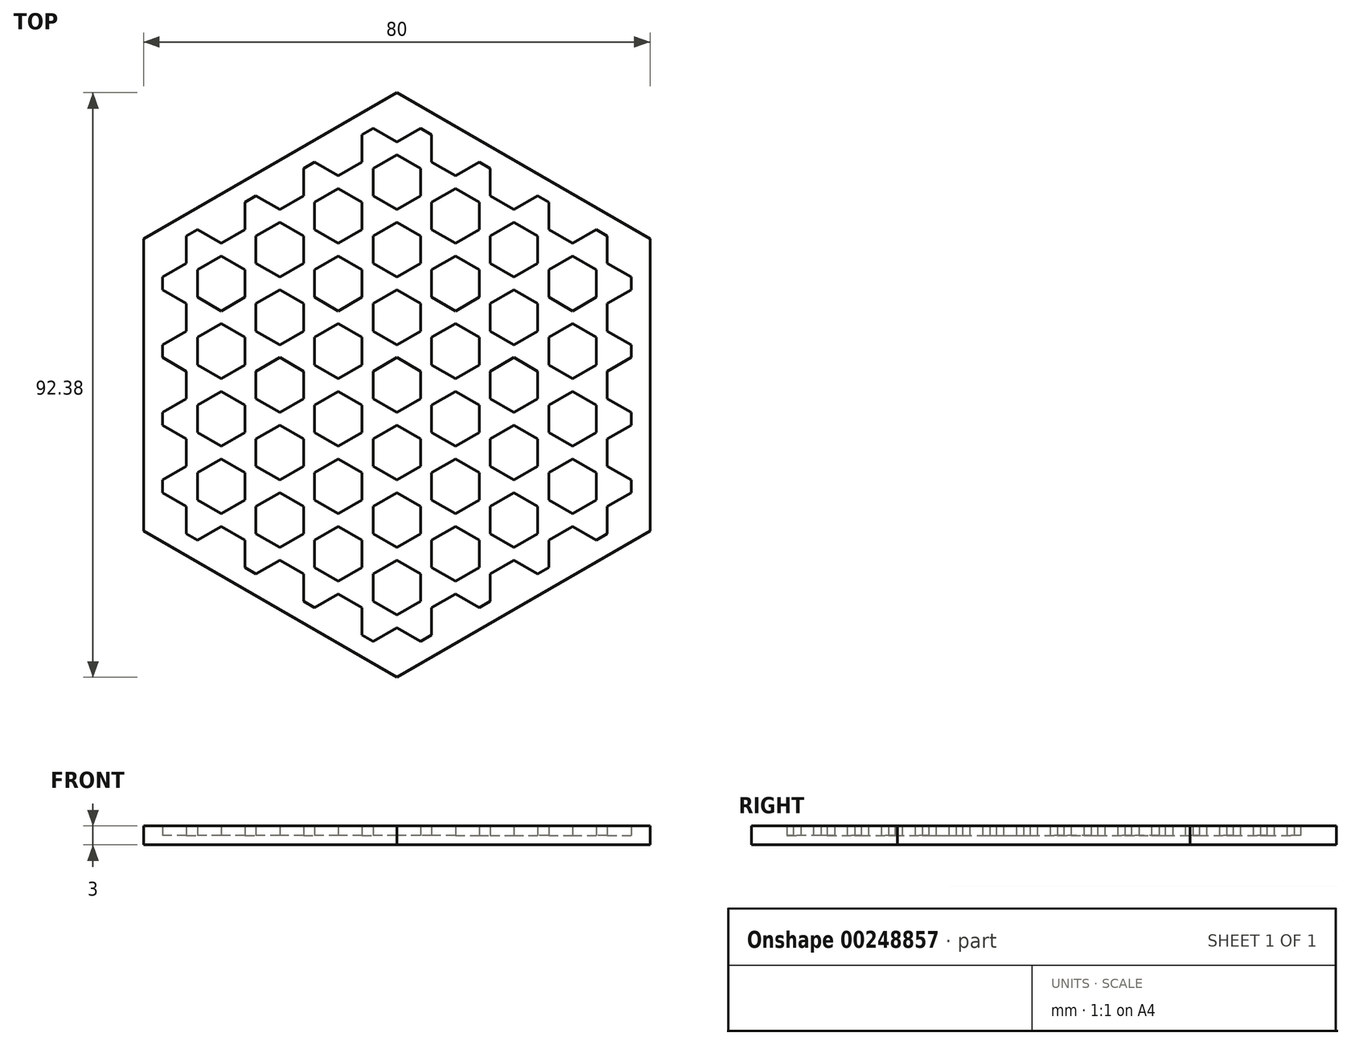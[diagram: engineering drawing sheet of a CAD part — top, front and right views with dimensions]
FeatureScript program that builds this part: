
annotation { "Feature Type Name" : "Feature", "Feature Type Description" : "" }
export const myFeature = defineFeature(function(context is Context, id is Id, definition is map)
    precondition{}
    {
        {
            var Q0;
            Q0=qCreatedBy(makeId("Top.planeOp"),FACE);
            var sketch = newSketch(context, id + "F0", { "sketchPlane" : qUnion([Q0])});
            skCircle(sketch, "E0.cCircle", {"center": v(0, 0) * mm, "radius": 40 * mm, "construction": true});
            skLineSegment(sketch, "E0.0", {"start": v(40, 23.1) * mm, "end": v(40, -23.1) * mm});
            skLineSegment(sketch, "E0.1", {"start": v(40, -23.1) * mm, "end": v(0, -46.19) * mm});
            skLineSegment(sketch, "E0.2", {"start": v(0, -46.19) * mm, "end": v(-40, -23.1) * mm});
            skLineSegment(sketch, "E0.3", {"start": v(-40, -23.1) * mm, "end": v(-40, 23.1) * mm});
            skLineSegment(sketch, "E0.4", {"start": v(-40, 23.1) * mm, "end": v(0, 46.19) * mm});
            skLineSegment(sketch, "E0.5", {"start": v(0, 46.19) * mm, "end": v(40, 23.1) * mm});
            skPoint(sketch, "E0.0.midPoint", {"position": v(40, 0) * mm});
            skSolve(sketch);
        }
        {
            var Q0;
            Q0=makeQuery(id+"F0.imprint","IMPRINT",FACE,{"disambiguationData":[TD([[makeQuery(id+"F0.imprint","IMPRINT",EDGE,{"derivedFrom":sQuery(id+"F0.wireOp",EDGE,"E0.0")}),-1.0]])]});
            extrude(context, id + "F3", {"entities" : qUnion([Q0]), "depth" : 3 * mm});
        }
        {
            var Q0;
            Q0=makeQuery(id+"F3.opExtrude","CAP_FACE",FACE,{"disambiguationData":[OSD([sQuery(id+"F0.wireOp",EDGE,"E0.0"),sQuery(id+"F0.wireOp",EDGE,"E0.1"),sQuery(id+"F0.wireOp",EDGE,"E0.2"),sQuery(id+"F0.wireOp",EDGE,"E0.3"),sQuery(id+"F0.wireOp",EDGE,"E0.4"),sQuery(id+"F0.wireOp",EDGE,"E0.5")])],"isStart":false});
            var sketch = newSketch(context, id + "F1", { "sketchPlane" : qUnion([Q0])});
            skCircle(sketch, "E1.cCircle", {"center": v(0, 0) * mm, "radius": 37 * mm, "construction": true});
            skPoint(sketch, "E1.cCircle.perimeterSnap0", {"position": v(40, 0) * mm});
            skLineSegment(sketch, "E1.0", {"start": v(37, 21.36) * mm, "end": v(37, -21.36) * mm});
            skLineSegment(sketch, "E1.1", {"start": v(37, -21.36) * mm, "end": v(0, -42.72) * mm});
            skLineSegment(sketch, "E1.2", {"start": v(0, -42.72) * mm, "end": v(-37, -21.36) * mm});
            skLineSegment(sketch, "E1.3", {"start": v(-37, -21.36) * mm, "end": v(-37, 21.36) * mm});
            skLineSegment(sketch, "E1.4", {"start": v(-37, 21.36) * mm, "end": v(0, 42.72) * mm});
            skLineSegment(sketch, "E1.5", {"start": v(0, 42.72) * mm, "end": v(37, 21.36) * mm});
            skPoint(sketch, "E1.0.midPoint", {"position": v(37, 0) * mm});
            skPoint(sketch, "E1.0.midPoint.positionSnap0", {"position": v(40, 0) * mm});
            skSolve(sketch);
        }
        {
            var Q0;
            Q0=makeQuery(id+"F1.imprint","IMPRINT",FACE,{"disambiguationData":[TD([[makeQuery(id+"F1.imprint","IMPRINT",EDGE,{"derivedFrom":sQuery(id+"F1.wireOp",EDGE,"E1.0")}),-1.0]])]});
            extrude(context, id + "F4", {"entities" : qUnion([Q0]), "operationType" : NewBodyOperationType.REMOVE, "oppositeDirection" : true, "depth" : 1.5 * mm});
        }
        {
            var Q0;
            Q0=makeQuery(id+"F4.boolean.opBoolean","COPY",FACE,{"derivedFrom":makeQuery(id+"F4.opExtrude","CAP_FACE",FACE,{"disambiguationData":[OSD([sQuery(id+"F1.wireOp",EDGE,"E1.0"),sQuery(id+"F1.wireOp",EDGE,"E1.1"),sQuery(id+"F1.wireOp",EDGE,"E1.2"),sQuery(id+"F1.wireOp",EDGE,"E1.3"),sQuery(id+"F1.wireOp",EDGE,"E1.4"),sQuery(id+"F1.wireOp",EDGE,"E1.5")])],"isStart":false})});
            var sketch = newSketch(context, id + "F2", { "sketchPlane" : qUnion([Q0])});
            skLineSegment(sketch, "E2", {"start": v(-32.37, 24.03) * mm, "end": v(-32.37, -24.03) * mm, "construction": true});
            skLineSegment(sketch, "E3", {"start": v(-23.12, 29.37) * mm, "end": v(-23.12, -29.37) * mm, "construction": true});
            skLineSegment(sketch, "E4", {"start": v(-13.88, 34.71) * mm, "end": v(-13.88, -34.71) * mm, "construction": true});
            skLineSegment(sketch, "E5", {"start": v(-4.62, 40.05) * mm, "end": v(-4.62, -40.05) * mm, "construction": true});
            skLineSegment(sketch, "E6", {"start": v(-37, -16.02) * mm, "end": v(4.63, -40.05) * mm, "construction": true});
            skLineSegment(sketch, "E7", {"start": v(13.88, -34.71) * mm, "end": v(-37, -5.34) * mm, "construction": true});
            skLineSegment(sketch, "E8", {"start": v(-37, 5.34) * mm, "end": v(23.12, -29.37) * mm, "construction": true});
            skLineSegment(sketch, "E9", {"start": v(32.37, -24.03) * mm, "end": v(-37, 16.02) * mm, "construction": true});
            skLineSegment(sketch, "E10", {"start": v(-32.37, 24.03) * mm, "end": v(37, -16.02) * mm, "construction": true});
            skLineSegment(sketch, "E11", {"start": v(-23.12, 29.37) * mm, "end": v(37, -5.34) * mm, "construction": true});
            skPoint(sketch, "E11.endSnap0", {"position": v(58.53, 6.8) * mm});
            skLineSegment(sketch, "E12", {"start": v(-13.88, 34.71) * mm, "end": v(37, 5.34) * mm, "construction": true});
            skLineSegment(sketch, "E13", {"start": v(-4.63, 40.05) * mm, "end": v(37, 16.02) * mm, "construction": true});
            skLineSegment(sketch, "E14", {"start": v(4.63, -40.05) * mm, "end": v(4.62, 40.05) * mm, "construction": true});
            skLineSegment(sketch, "E15", {"start": v(13.88, -34.71) * mm, "end": v(13.87, 34.71) * mm, "construction": true});
            skLineSegment(sketch, "E16", {"start": v(23.12, -29.37) * mm, "end": v(23.12, 29.37) * mm, "construction": true});
            skLineSegment(sketch, "E17", {"start": v(32.37, -24.03) * mm, "end": v(32.37, 24.03) * mm, "construction": true});
            skLineSegment(sketch, "E18", {"start": v(-37, 16.02) * mm, "end": v(4.63, 40.05) * mm, "construction": true});
            skLineSegment(sketch, "E19", {"start": v(-37, 5.34) * mm, "end": v(13.88, 34.71) * mm, "construction": true});
            skLineSegment(sketch, "E20", {"start": v(-37, -5.34) * mm, "end": v(23.12, 29.37) * mm, "construction": true});
            skLineSegment(sketch, "E21", {"start": v(-37, -16.02) * mm, "end": v(32.37, 24.03) * mm, "construction": true});
            skLineSegment(sketch, "E22", {"start": v(-32.37, -24.03) * mm, "end": v(37, 16.02) * mm, "construction": true});
            skLineSegment(sketch, "E23", {"start": v(37, 5.34) * mm, "end": v(-23.12, -29.37) * mm, "construction": true});
            skLineSegment(sketch, "E24", {"start": v(-13.88, -34.71) * mm, "end": v(37, -5.34) * mm, "construction": true});
            skLineSegment(sketch, "E25", {"start": v(-4.62, -40.05) * mm, "end": v(37, -16.02) * mm, "construction": true});
            skSolve(sketch);
        }
        {
            var Q0;
            Q0=makeQuery(id+"F4.boolean.opBoolean","COPY",FACE,{"derivedFrom":makeQuery(id+"F4.opExtrude","CAP_FACE",FACE,{"disambiguationData":[OSD([sQuery(id+"F1.wireOp",EDGE,"E1.0"),sQuery(id+"F1.wireOp",EDGE,"E1.1"),sQuery(id+"F1.wireOp",EDGE,"E1.2"),sQuery(id+"F1.wireOp",EDGE,"E1.3"),sQuery(id+"F1.wireOp",EDGE,"E1.4"),sQuery(id+"F1.wireOp",EDGE,"E1.5")])],"isStart":false})});
            var sketch = newSketch(context, id + "F5", { "sketchPlane" : qUnion([Q0])});
            skCircle(sketch, "E26.cCircle", {"center": v(0, 0) * mm, "radius": 3.75 * mm, "construction": true});
            skLineSegment(sketch, "E26.0", {"start": v(3.75, 2.17) * mm, "end": v(3.75, -2.17) * mm});
            skLineSegment(sketch, "E26.1", {"start": v(3.75, -2.17) * mm, "end": v(0, -4.33) * mm});
            skLineSegment(sketch, "E26.2", {"start": v(0, -4.33) * mm, "end": v(-3.75, -2.17) * mm});
            skLineSegment(sketch, "E26.3", {"start": v(-3.75, -2.17) * mm, "end": v(-3.75, 2.17) * mm});
            skLineSegment(sketch, "E26.4", {"start": v(-3.75, 2.17) * mm, "end": v(0, 4.33) * mm});
            skLineSegment(sketch, "E26.5", {"start": v(0, 4.33) * mm, "end": v(3.75, 2.17) * mm});
            skPoint(sketch, "E26.0.midPoint", {"position": v(3.75, 0) * mm});
            skCircle(sketch, "E27.cCircle", {"center": v(0, -10.68) * mm, "radius": 3.75 * mm, "construction": true});
            skLineSegment(sketch, "E27.0", {"start": v(3.75, -8.52) * mm, "end": v(3.75, -12.85) * mm});
            skLineSegment(sketch, "E27.1", {"start": v(3.75, -12.85) * mm, "end": v(0, -15.01) * mm});
            skLineSegment(sketch, "E27.2", {"start": v(0, -15.01) * mm, "end": v(-3.75, -12.85) * mm});
            skLineSegment(sketch, "E27.3", {"start": v(-3.75, -12.85) * mm, "end": v(-3.75, -8.52) * mm});
            skLineSegment(sketch, "E27.4", {"start": v(-3.75, -8.52) * mm, "end": v(0, -6.35) * mm});
            skLineSegment(sketch, "E27.5", {"start": v(0, -6.35) * mm, "end": v(3.75, -8.52) * mm});
            skPoint(sketch, "E27.0.midPoint", {"position": v(3.75, -10.68) * mm});
            skCircle(sketch, "E28.cCircle", {"center": v(0, -21.36) * mm, "radius": 3.75 * mm, "construction": true});
            skLineSegment(sketch, "E28.0", {"start": v(3.75, -19.2) * mm, "end": v(3.75, -23.53) * mm});
            skLineSegment(sketch, "E28.1", {"start": v(3.75, -23.53) * mm, "end": v(0, -25.7) * mm});
            skLineSegment(sketch, "E28.2", {"start": v(0, -25.7) * mm, "end": v(-3.75, -23.53) * mm});
            skLineSegment(sketch, "E28.3", {"start": v(-3.75, -23.53) * mm, "end": v(-3.75, -19.2) * mm});
            skLineSegment(sketch, "E28.4", {"start": v(-3.75, -19.2) * mm, "end": v(0, -17.03) * mm});
            skLineSegment(sketch, "E28.5", {"start": v(0, -17.03) * mm, "end": v(3.75, -19.2) * mm});
            skPoint(sketch, "E28.0.midPoint", {"position": v(3.75, -21.36) * mm});
            skCircle(sketch, "E29.cCircle", {"center": v(0, -32.04) * mm, "radius": 3.75 * mm, "construction": true});
            skLineSegment(sketch, "E29.0", {"start": v(3.75, -29.88) * mm, "end": v(3.75, -34.2) * mm});
            skLineSegment(sketch, "E29.1", {"start": v(3.75, -34.2) * mm, "end": v(0, -36.37) * mm});
            skLineSegment(sketch, "E29.2", {"start": v(0, -36.37) * mm, "end": v(-3.75, -34.2) * mm});
            skLineSegment(sketch, "E29.3", {"start": v(-3.75, -34.2) * mm, "end": v(-3.75, -29.88) * mm});
            skLineSegment(sketch, "E29.4", {"start": v(-3.75, -29.88) * mm, "end": v(0, -27.71) * mm});
            skLineSegment(sketch, "E29.5", {"start": v(0, -27.71) * mm, "end": v(3.75, -29.88) * mm});
            skPoint(sketch, "E29.0.midPoint", {"position": v(3.75, -32.04) * mm});
            skCircle(sketch, "E30.cCircle", {"center": v(0, -42.72) * mm, "radius": 3.75 * mm, "construction": true});
            skLineSegment(sketch, "E30.0", {"start": v(3.75, -40.56) * mm, "end": v(3.75, -44.89) * mm});
            skLineSegment(sketch, "E30.1", {"start": v(3.75, -44.89) * mm, "end": v(0, -47.05) * mm});
            skLineSegment(sketch, "E30.2", {"start": v(0, -47.05) * mm, "end": v(-3.75, -44.89) * mm});
            skLineSegment(sketch, "E30.3", {"start": v(-3.75, -44.89) * mm, "end": v(-3.75, -40.56) * mm});
            skLineSegment(sketch, "E30.4", {"start": v(-3.75, -40.56) * mm, "end": v(0, -38.4) * mm});
            skLineSegment(sketch, "E30.5", {"start": v(0, -38.4) * mm, "end": v(3.75, -40.56) * mm});
            skPoint(sketch, "E30.0.midPoint", {"position": v(3.75, -42.72) * mm});
            skLineSegment(sketch, "E31", {"start": v(-37, -5.34) * mm, "end": v(-37, -16.02) * mm, "construction": true});
            skLineSegment(sketch, "E32", {"start": v(-37, -10.68) * mm, "end": v(37, -10.68) * mm, "construction": true});
            skLineSegment(sketch, "E33", {"start": v(0, 0) * mm, "end": v(0, -10.68) * mm, "construction": true});
            skLineSegment(sketch, "E34", {"start": v(0, -10.68) * mm, "end": v(0, -21.36) * mm, "construction": true});
            skLineSegment(sketch, "E35", {"start": v(0, -21.36) * mm, "end": v(0, -32.04) * mm, "construction": true});
            skLineSegment(sketch, "E36", {"start": v(0, -32.04) * mm, "end": v(0, -42.72) * mm, "construction": true});
            skCircle(sketch, "E37.cCircle", {"center": v(0, 10.68) * mm, "radius": 3.75 * mm, "construction": true});
            skLineSegment(sketch, "E37.0", {"start": v(3.75, 12.85) * mm, "end": v(3.75, 8.52) * mm});
            skLineSegment(sketch, "E37.1", {"start": v(3.75, 8.52) * mm, "end": v(0, 6.35) * mm});
            skLineSegment(sketch, "E37.2", {"start": v(0, 6.35) * mm, "end": v(-3.75, 8.52) * mm});
            skLineSegment(sketch, "E37.3", {"start": v(-3.75, 8.52) * mm, "end": v(-3.75, 12.85) * mm});
            skLineSegment(sketch, "E37.4", {"start": v(-3.75, 12.85) * mm, "end": v(0, 15.01) * mm});
            skLineSegment(sketch, "E37.5", {"start": v(0, 15.01) * mm, "end": v(3.75, 12.85) * mm});
            skPoint(sketch, "E37.0.midPoint", {"position": v(3.75, 10.68) * mm});
            skCircle(sketch, "E38.cCircle", {"center": v(0, 21.36) * mm, "radius": 3.75 * mm, "construction": true});
            skLineSegment(sketch, "E38.0", {"start": v(3.75, 23.53) * mm, "end": v(3.75, 19.2) * mm});
            skLineSegment(sketch, "E38.1", {"start": v(3.75, 19.2) * mm, "end": v(0, 17.03) * mm});
            skLineSegment(sketch, "E38.2", {"start": v(0, 17.03) * mm, "end": v(-3.75, 19.2) * mm});
            skLineSegment(sketch, "E38.3", {"start": v(-3.75, 19.2) * mm, "end": v(-3.75, 23.53) * mm});
            skLineSegment(sketch, "E38.4", {"start": v(-3.75, 23.53) * mm, "end": v(0, 25.7) * mm});
            skLineSegment(sketch, "E38.5", {"start": v(0, 25.7) * mm, "end": v(3.75, 23.53) * mm});
            skPoint(sketch, "E38.0.midPoint", {"position": v(3.75, 21.36) * mm});
            skCircle(sketch, "E39.cCircle", {"center": v(0, 32.04) * mm, "radius": 3.75 * mm, "construction": true});
            skLineSegment(sketch, "E39.0", {"start": v(3.75, 34.2) * mm, "end": v(3.75, 29.88) * mm});
            skLineSegment(sketch, "E39.1", {"start": v(3.75, 29.88) * mm, "end": v(0, 27.71) * mm});
            skLineSegment(sketch, "E39.2", {"start": v(0, 27.71) * mm, "end": v(-3.75, 29.88) * mm});
            skLineSegment(sketch, "E39.3", {"start": v(-3.75, 29.88) * mm, "end": v(-3.75, 34.2) * mm});
            skLineSegment(sketch, "E39.4", {"start": v(-3.75, 34.2) * mm, "end": v(0, 36.37) * mm});
            skLineSegment(sketch, "E39.5", {"start": v(0, 36.37) * mm, "end": v(3.75, 34.2) * mm});
            skPoint(sketch, "E39.0.midPoint", {"position": v(3.75, 32.04) * mm});
            skCircle(sketch, "E40.cCircle", {"center": v(0, 42.72) * mm, "radius": 3.75 * mm, "construction": true});
            skLineSegment(sketch, "E40.0", {"start": v(3.75, 44.89) * mm, "end": v(3.75, 40.56) * mm});
            skLineSegment(sketch, "E40.1", {"start": v(3.75, 40.56) * mm, "end": v(0, 38.4) * mm});
            skLineSegment(sketch, "E40.2", {"start": v(0, 38.4) * mm, "end": v(-3.75, 40.56) * mm});
            skLineSegment(sketch, "E40.3", {"start": v(-3.75, 40.56) * mm, "end": v(-3.75, 44.89) * mm});
            skLineSegment(sketch, "E40.4", {"start": v(-3.75, 44.89) * mm, "end": v(0, 47.05) * mm});
            skLineSegment(sketch, "E40.5", {"start": v(0, 47.05) * mm, "end": v(3.75, 44.89) * mm});
            skPoint(sketch, "E40.0.midPoint", {"position": v(3.75, 42.72) * mm});
            skLineSegment(sketch, "E41", {"start": v(0, 42.72) * mm, "end": v(0, 32.04) * mm, "construction": true});
            skLineSegment(sketch, "E42", {"start": v(0, 21.36) * mm, "end": v(0, 32.04) * mm, "construction": true});
            skLineSegment(sketch, "E43", {"start": v(0, 21.36) * mm, "end": v(0, 10.68) * mm, "construction": true});
            skLineSegment(sketch, "E44", {"start": v(0, 10.68) * mm, "end": v(0, 0) * mm, "construction": true});
            skLineSegment(sketch, "E45", {"start": v(-37, -5.34) * mm, "end": v(37, -5.34) * mm, "construction": true});
            skCircle(sketch, "E46.cCircle", {"center": v(-9.25, -5.34) * mm, "radius": 3.75 * mm, "construction": true});
            skLineSegment(sketch, "E46.0", {"start": v(-5.5, -3.18) * mm, "end": v(-5.5, -7.5) * mm});
            skLineSegment(sketch, "E46.1", {"start": v(-5.5, -7.5) * mm, "end": v(-9.25, -9.67) * mm});
            skLineSegment(sketch, "E46.2", {"start": v(-9.25, -9.67) * mm, "end": v(-13, -7.5) * mm});
            skLineSegment(sketch, "E46.3", {"start": v(-13, -7.5) * mm, "end": v(-13, -3.18) * mm});
            skLineSegment(sketch, "E46.4", {"start": v(-13, -3.18) * mm, "end": v(-9.25, -1.01) * mm});
            skLineSegment(sketch, "E46.5", {"start": v(-9.25, -1.01) * mm, "end": v(-5.5, -3.18) * mm});
            skPoint(sketch, "E46.0.midPoint", {"position": v(-5.5, -5.34) * mm});
            skCircle(sketch, "E47.cCircle", {"center": v(-9.25, -16.02) * mm, "radius": 3.75 * mm, "construction": true});
            skLineSegment(sketch, "E47.0", {"start": v(-13, -18.19) * mm, "end": v(-13, -13.86) * mm});
            skLineSegment(sketch, "E47.1", {"start": v(-13, -13.86) * mm, "end": v(-9.25, -11.7) * mm});
            skLineSegment(sketch, "E47.2", {"start": v(-9.25, -11.7) * mm, "end": v(-5.5, -13.86) * mm});
            skLineSegment(sketch, "E47.3", {"start": v(-5.5, -13.86) * mm, "end": v(-5.5, -18.19) * mm});
            skLineSegment(sketch, "E47.4", {"start": v(-5.5, -18.19) * mm, "end": v(-9.25, -20.35) * mm});
            skLineSegment(sketch, "E47.5", {"start": v(-9.25, -20.35) * mm, "end": v(-13, -18.19) * mm});
            skPoint(sketch, "E47.0.midPoint", {"position": v(-13, -16.02) * mm});
            skCircle(sketch, "E48.cCircle", {"center": v(-9.25, -26.7) * mm, "radius": 3.75 * mm, "construction": true});
            skLineSegment(sketch, "E48.0", {"start": v(-13, -28.87) * mm, "end": v(-13, -24.54) * mm});
            skLineSegment(sketch, "E48.1", {"start": v(-13, -24.54) * mm, "end": v(-9.25, -22.37) * mm});
            skLineSegment(sketch, "E48.2", {"start": v(-9.25, -22.37) * mm, "end": v(-5.5, -24.54) * mm});
            skLineSegment(sketch, "E48.3", {"start": v(-5.5, -24.54) * mm, "end": v(-5.5, -28.87) * mm});
            skLineSegment(sketch, "E48.4", {"start": v(-5.5, -28.87) * mm, "end": v(-9.25, -31.03) * mm});
            skLineSegment(sketch, "E48.5", {"start": v(-9.25, -31.03) * mm, "end": v(-13, -28.87) * mm});
            skPoint(sketch, "E48.0.midPoint", {"position": v(-13, -26.7) * mm});
            skCircle(sketch, "E49.cCircle", {"center": v(-9.25, -37.38) * mm, "radius": 3.75 * mm, "construction": true});
            skLineSegment(sketch, "E49.0", {"start": v(-13, -39.55) * mm, "end": v(-13, -35.22) * mm});
            skLineSegment(sketch, "E49.1", {"start": v(-13, -35.22) * mm, "end": v(-9.25, -33.05) * mm});
            skLineSegment(sketch, "E49.2", {"start": v(-9.25, -33.05) * mm, "end": v(-5.5, -35.22) * mm});
            skLineSegment(sketch, "E49.3", {"start": v(-5.5, -35.22) * mm, "end": v(-5.5, -39.55) * mm});
            skLineSegment(sketch, "E49.4", {"start": v(-5.5, -39.55) * mm, "end": v(-9.25, -41.71) * mm});
            skLineSegment(sketch, "E49.5", {"start": v(-9.25, -41.71) * mm, "end": v(-13, -39.55) * mm});
            skPoint(sketch, "E49.0.midPoint", {"position": v(-13, -37.38) * mm});
            skCircle(sketch, "E50.cCircle", {"center": v(-9.25, 5.34) * mm, "radius": 3.75 * mm, "construction": true});
            skLineSegment(sketch, "E50.0", {"start": v(-13, 3.18) * mm, "end": v(-13, 7.5) * mm});
            skLineSegment(sketch, "E50.1", {"start": v(-13, 7.5) * mm, "end": v(-9.25, 9.67) * mm});
            skLineSegment(sketch, "E50.2", {"start": v(-9.25, 9.67) * mm, "end": v(-5.5, 7.5) * mm});
            skLineSegment(sketch, "E50.3", {"start": v(-5.5, 7.5) * mm, "end": v(-5.5, 3.18) * mm});
            skLineSegment(sketch, "E50.4", {"start": v(-5.5, 3.18) * mm, "end": v(-9.25, 1.01) * mm});
            skLineSegment(sketch, "E50.5", {"start": v(-9.25, 1.01) * mm, "end": v(-13, 3.18) * mm});
            skPoint(sketch, "E50.0.midPoint", {"position": v(-13, 5.34) * mm});
            skCircle(sketch, "E51.cCircle", {"center": v(-9.25, 16.02) * mm, "radius": 3.75 * mm, "construction": true});
            skLineSegment(sketch, "E51.0", {"start": v(-13, 13.86) * mm, "end": v(-13, 18.19) * mm});
            skLineSegment(sketch, "E51.1", {"start": v(-13, 18.19) * mm, "end": v(-9.25, 20.35) * mm});
            skLineSegment(sketch, "E51.2", {"start": v(-9.25, 20.35) * mm, "end": v(-5.5, 18.19) * mm});
            skLineSegment(sketch, "E51.3", {"start": v(-5.5, 18.19) * mm, "end": v(-5.5, 13.86) * mm});
            skLineSegment(sketch, "E51.4", {"start": v(-5.5, 13.86) * mm, "end": v(-9.25, 11.7) * mm});
            skLineSegment(sketch, "E51.5", {"start": v(-9.25, 11.7) * mm, "end": v(-13, 13.86) * mm});
            skPoint(sketch, "E51.0.midPoint", {"position": v(-13, 16.02) * mm});
            skCircle(sketch, "E52.cCircle", {"center": v(-9.25, 26.7) * mm, "radius": 3.75 * mm, "construction": true});
            skLineSegment(sketch, "E52.0", {"start": v(-13, 24.54) * mm, "end": v(-13, 28.87) * mm});
            skLineSegment(sketch, "E52.1", {"start": v(-13, 28.87) * mm, "end": v(-9.25, 31.03) * mm});
            skLineSegment(sketch, "E52.2", {"start": v(-9.25, 31.03) * mm, "end": v(-5.5, 28.87) * mm});
            skLineSegment(sketch, "E52.3", {"start": v(-5.5, 28.87) * mm, "end": v(-5.5, 24.54) * mm});
            skLineSegment(sketch, "E52.4", {"start": v(-5.5, 24.54) * mm, "end": v(-9.25, 22.37) * mm});
            skLineSegment(sketch, "E52.5", {"start": v(-9.25, 22.37) * mm, "end": v(-13, 24.54) * mm});
            skPoint(sketch, "E52.0.midPoint", {"position": v(-13, 26.7) * mm});
            skCircle(sketch, "E53.cCircle", {"center": v(-9.25, 37.38) * mm, "radius": 3.75 * mm, "construction": true});
            skLineSegment(sketch, "E53.0", {"start": v(-13, 35.22) * mm, "end": v(-13, 39.55) * mm});
            skLineSegment(sketch, "E53.1", {"start": v(-13, 39.55) * mm, "end": v(-9.25, 41.71) * mm});
            skLineSegment(sketch, "E53.2", {"start": v(-9.25, 41.71) * mm, "end": v(-5.5, 39.55) * mm});
            skLineSegment(sketch, "E53.3", {"start": v(-5.5, 39.55) * mm, "end": v(-5.5, 35.22) * mm});
            skLineSegment(sketch, "E53.4", {"start": v(-5.5, 35.22) * mm, "end": v(-9.25, 33.05) * mm});
            skLineSegment(sketch, "E53.5", {"start": v(-9.25, 33.05) * mm, "end": v(-13, 35.22) * mm});
            skPoint(sketch, "E53.0.midPoint", {"position": v(-13, 37.38) * mm});
            skLineSegment(sketch, "E54", {"start": v(-4.63, 40.05) * mm, "end": v(-13.88, 34.71) * mm, "construction": true});
            skLineSegment(sketch, "E55", {"start": v(-9.25, -5.34) * mm, "end": v(-9.25, 5.34) * mm, "construction": true});
            skLineSegment(sketch, "E56", {"start": v(-9.25, 5.34) * mm, "end": v(-9.25, 16.02) * mm, "construction": true});
            skLineSegment(sketch, "E57", {"start": v(-9.25, 16.02) * mm, "end": v(-9.25, 26.7) * mm, "construction": true});
            skLineSegment(sketch, "E58", {"start": v(-9.25, 26.7) * mm, "end": v(-9.25, 37.38) * mm, "construction": true});
            skLineSegment(sketch, "E59", {"start": v(-9.25, -5.34) * mm, "end": v(-9.25, -16.02) * mm, "construction": true});
            skLineSegment(sketch, "E60", {"start": v(-9.25, -16.02) * mm, "end": v(-9.25, -26.7) * mm, "construction": true});
            skLineSegment(sketch, "E61", {"start": v(-9.25, -26.7) * mm, "end": v(-9.25, -37.38) * mm, "construction": true});
            skLineSegment(sketch, "E62.1.0.0", {"start": v(22.25, -34.2) * mm, "end": v(18.5, -36.37) * mm});
            skLineSegment(sketch, "E62.1.0.1", {"start": v(22.25, 34.2) * mm, "end": v(22.25, 29.88) * mm});
            skLineSegment(sketch, "E62.1.0.2", {"start": v(14.75, 12.85) * mm, "end": v(18.5, 15.01) * mm});
            skLineSegment(sketch, "E62.1.0.3", {"start": v(18.5, -4.33) * mm, "end": v(14.75, -2.17) * mm});
            skLineSegment(sketch, "E62.1.0.4", {"start": v(22.25, 12.85) * mm, "end": v(22.25, 8.52) * mm});
            skLineSegment(sketch, "E62.1.0.5", {"start": v(14.75, -8.52) * mm, "end": v(18.5, -6.35) * mm});
            skLineSegment(sketch, "E62.1.0.6", {"start": v(18.5, 17.03) * mm, "end": v(14.75, 19.2) * mm});
            skLineSegment(sketch, "E62.1.0.7", {"start": v(18.5, 27.71) * mm, "end": v(14.75, 29.88) * mm});
            skLineSegment(sketch, "E62.1.0.8", {"start": v(14.75, -19.2) * mm, "end": v(18.5, -17.03) * mm});
            skLineSegment(sketch, "E62.1.0.9", {"start": v(14.75, 29.88) * mm, "end": v(14.75, 34.2) * mm});
            skLineSegment(sketch, "E62.1.0.10", {"start": v(18.5, 36.37) * mm, "end": v(22.25, 34.2) * mm});
            skLineSegment(sketch, "E62.1.0.11", {"start": v(14.75, 19.2) * mm, "end": v(14.75, 23.53) * mm});
            skLineSegment(sketch, "E62.1.0.12", {"start": v(22.25, 23.53) * mm, "end": v(22.25, 19.2) * mm});
            skLineSegment(sketch, "E62.1.0.13", {"start": v(14.75, -23.53) * mm, "end": v(14.75, -19.2) * mm});
            skLineSegment(sketch, "E62.1.0.14", {"start": v(22.25, -12.85) * mm, "end": v(18.5, -15.01) * mm});
            skLineSegment(sketch, "E62.1.0.15", {"start": v(14.75, 8.52) * mm, "end": v(14.75, 12.85) * mm});
            skLineSegment(sketch, "E62.1.0.16", {"start": v(22.25, 19.2) * mm, "end": v(18.5, 17.03) * mm});
            skLineSegment(sketch, "E62.1.0.17", {"start": v(18.5, 15.01) * mm, "end": v(22.25, 12.85) * mm});
            skLineSegment(sketch, "E62.1.0.18", {"start": v(14.75, -34.2) * mm, "end": v(14.75, -29.88) * mm});
            skLineSegment(sketch, "E62.1.0.19", {"start": v(14.75, 23.53) * mm, "end": v(18.5, 25.7) * mm});
            skLineSegment(sketch, "E62.1.0.20", {"start": v(14.75, -12.85) * mm, "end": v(14.75, -8.52) * mm});
            skLineSegment(sketch, "E62.1.0.21", {"start": v(18.5, -15.01) * mm, "end": v(14.75, -12.85) * mm});
            skLineSegment(sketch, "E62.1.0.22", {"start": v(22.25, -29.88) * mm, "end": v(22.25, -34.2) * mm});
            skLineSegment(sketch, "E62.1.0.23", {"start": v(22.25, -19.2) * mm, "end": v(22.25, -23.53) * mm});
            skLineSegment(sketch, "E62.1.0.24", {"start": v(22.25, -23.53) * mm, "end": v(18.5, -25.7) * mm});
            skLineSegment(sketch, "E62.1.0.25", {"start": v(18.5, -36.37) * mm, "end": v(14.75, -34.2) * mm});
            skLineSegment(sketch, "E62.1.0.26", {"start": v(18.5, -25.7) * mm, "end": v(14.75, -23.53) * mm});
            skLineSegment(sketch, "E62.1.0.27", {"start": v(22.25, 29.88) * mm, "end": v(18.5, 27.71) * mm});
            skLineSegment(sketch, "E62.1.0.28", {"start": v(18.5, 6.35) * mm, "end": v(14.75, 8.52) * mm});
            skLineSegment(sketch, "E62.1.0.29", {"start": v(18.5, -27.71) * mm, "end": v(22.25, -29.88) * mm});
            skLineSegment(sketch, "E62.1.0.30", {"start": v(14.75, -29.88) * mm, "end": v(18.5, -27.71) * mm});
            skLineSegment(sketch, "E62.1.0.31", {"start": v(14.75, -2.17) * mm, "end": v(14.75, 2.17) * mm});
            skLineSegment(sketch, "E62.1.0.32", {"start": v(22.25, -2.17) * mm, "end": v(18.5, -4.33) * mm});
            skLineSegment(sketch, "E62.1.0.33", {"start": v(14.75, 34.2) * mm, "end": v(18.5, 36.37) * mm});
            skLineSegment(sketch, "E62.1.0.34", {"start": v(18.5, -6.35) * mm, "end": v(22.25, -8.52) * mm});
            skLineSegment(sketch, "E62.1.0.35", {"start": v(22.25, 8.52) * mm, "end": v(18.5, 6.35) * mm});
            skLineSegment(sketch, "E62.1.0.36", {"start": v(14.75, 2.17) * mm, "end": v(18.5, 4.33) * mm});
            skLineSegment(sketch, "E62.1.0.37", {"start": v(22.25, -8.52) * mm, "end": v(22.25, -12.85) * mm});
            skLineSegment(sketch, "E62.1.0.38", {"start": v(18.5, 4.33) * mm, "end": v(22.25, 2.17) * mm});
            skLineSegment(sketch, "E62.1.0.39", {"start": v(18.5, -17.03) * mm, "end": v(22.25, -19.2) * mm});
            skLineSegment(sketch, "E62.1.0.40", {"start": v(18.5, 25.7) * mm, "end": v(22.25, 23.53) * mm});
            skLineSegment(sketch, "E62.1.0.41", {"start": v(22.25, 2.17) * mm, "end": v(22.25, -2.17) * mm});
            skLineSegment(sketch, "E62.2.0.2", {"start": v(33.25, 12.85) * mm, "end": v(37, 15.01) * mm});
            skLineSegment(sketch, "E62.2.0.3", {"start": v(37, -4.33) * mm, "end": v(33.25, -2.17) * mm});
            skLineSegment(sketch, "E62.2.0.4", {"start": v(40.75, 12.85) * mm, "end": v(40.75, 8.52) * mm});
            skLineSegment(sketch, "E62.2.0.5", {"start": v(33.25, -8.52) * mm, "end": v(37, -6.35) * mm});
            skLineSegment(sketch, "E62.2.0.6", {"start": v(37, 17.03) * mm, "end": v(33.25, 19.2) * mm});
            skLineSegment(sketch, "E62.2.0.8", {"start": v(33.25, -19.2) * mm, "end": v(37, -17.03) * mm});
            skLineSegment(sketch, "E62.2.0.11", {"start": v(33.25, 19.2) * mm, "end": v(33.25, 23.53) * mm});
            skLineSegment(sketch, "E62.2.0.12", {"start": v(40.75, 23.53) * mm, "end": v(40.75, 19.2) * mm});
            skLineSegment(sketch, "E62.2.0.13", {"start": v(33.25, -23.53) * mm, "end": v(33.25, -19.2) * mm});
            skLineSegment(sketch, "E62.2.0.14", {"start": v(40.75, -12.85) * mm, "end": v(37, -15.01) * mm});
            skLineSegment(sketch, "E62.2.0.15", {"start": v(33.25, 8.52) * mm, "end": v(33.25, 12.85) * mm});
            skLineSegment(sketch, "E62.2.0.16", {"start": v(40.75, 19.2) * mm, "end": v(37, 17.03) * mm});
            skLineSegment(sketch, "E62.2.0.17", {"start": v(37, 15.01) * mm, "end": v(40.75, 12.85) * mm});
            skLineSegment(sketch, "E62.2.0.19", {"start": v(33.25, 23.53) * mm, "end": v(37, 25.7) * mm});
            skLineSegment(sketch, "E62.2.0.20", {"start": v(33.25, -12.85) * mm, "end": v(33.25, -8.52) * mm});
            skLineSegment(sketch, "E62.2.0.21", {"start": v(37, -15.01) * mm, "end": v(33.25, -12.85) * mm});
            skLineSegment(sketch, "E62.2.0.23", {"start": v(40.75, -19.2) * mm, "end": v(40.75, -23.53) * mm});
            skLineSegment(sketch, "E62.2.0.24", {"start": v(40.75, -23.53) * mm, "end": v(37, -25.7) * mm});
            skLineSegment(sketch, "E62.2.0.26", {"start": v(37, -25.7) * mm, "end": v(33.25, -23.53) * mm});
            skLineSegment(sketch, "E62.2.0.28", {"start": v(37, 6.35) * mm, "end": v(33.25, 8.52) * mm});
            skLineSegment(sketch, "E62.2.0.31", {"start": v(33.25, -2.17) * mm, "end": v(33.25, 2.17) * mm});
            skLineSegment(sketch, "E62.2.0.32", {"start": v(40.75, -2.17) * mm, "end": v(37, -4.33) * mm});
            skLineSegment(sketch, "E62.2.0.34", {"start": v(37, -6.35) * mm, "end": v(40.75, -8.52) * mm});
            skLineSegment(sketch, "E62.2.0.35", {"start": v(40.75, 8.52) * mm, "end": v(37, 6.35) * mm});
            skLineSegment(sketch, "E62.2.0.36", {"start": v(33.25, 2.17) * mm, "end": v(37, 4.33) * mm});
            skLineSegment(sketch, "E62.2.0.37", {"start": v(40.75, -8.52) * mm, "end": v(40.75, -12.85) * mm});
            skLineSegment(sketch, "E62.2.0.38", {"start": v(37, 4.33) * mm, "end": v(40.75, 2.17) * mm});
            skLineSegment(sketch, "E62.2.0.39", {"start": v(37, -17.03) * mm, "end": v(40.75, -19.2) * mm});
            skLineSegment(sketch, "E62.2.0.40", {"start": v(37, 25.7) * mm, "end": v(40.75, 23.53) * mm});
            skLineSegment(sketch, "E62.2.0.41", {"start": v(40.75, 2.17) * mm, "end": v(40.75, -2.17) * mm});
            skLineSegment(sketch, "E62.direction1", {"start": v(-3.75, -34.2) * mm, "end": v(14.75, -34.2) * mm, "construction": true});
            skLineSegment(sketch, "E63.1.0.0", {"start": v(13, -13.86) * mm, "end": v(13, -18.19) * mm});
            skLineSegment(sketch, "E63.1.0.1", {"start": v(9.25, -11.7) * mm, "end": v(13, -13.86) * mm});
            skLineSegment(sketch, "E63.1.0.2", {"start": v(5.5, 28.87) * mm, "end": v(9.25, 31.03) * mm});
            skLineSegment(sketch, "E63.1.0.3", {"start": v(9.25, -20.35) * mm, "end": v(5.5, -18.19) * mm});
            skLineSegment(sketch, "E63.1.0.4", {"start": v(13, -28.87) * mm, "end": v(9.25, -31.03) * mm});
            skLineSegment(sketch, "E63.1.0.5", {"start": v(5.5, 3.18) * mm, "end": v(5.5, 7.5) * mm});
            skLineSegment(sketch, "E63.1.0.6", {"start": v(9.25, 11.7) * mm, "end": v(5.5, 13.86) * mm});
            skLineSegment(sketch, "E63.1.0.7", {"start": v(5.5, 24.54) * mm, "end": v(5.5, 28.87) * mm});
            skLineSegment(sketch, "E63.1.0.8", {"start": v(13, -18.19) * mm, "end": v(9.25, -20.35) * mm});
            skLineSegment(sketch, "E63.1.0.9", {"start": v(9.25, -9.67) * mm, "end": v(5.5, -7.5) * mm});
            skLineSegment(sketch, "E63.1.0.10", {"start": v(13, -3.18) * mm, "end": v(13, -7.5) * mm});
            skLineSegment(sketch, "E63.1.0.11", {"start": v(13, 3.18) * mm, "end": v(9.25, 1.01) * mm});
            skLineSegment(sketch, "E63.1.0.12", {"start": v(13, -7.5) * mm, "end": v(9.25, -9.67) * mm});
            skLineSegment(sketch, "E63.1.0.13", {"start": v(13, -24.54) * mm, "end": v(13, -28.87) * mm});
            skLineSegment(sketch, "E63.1.0.14", {"start": v(9.25, 1.01) * mm, "end": v(5.5, 3.18) * mm});
            skLineSegment(sketch, "E63.1.0.15", {"start": v(9.25, 22.37) * mm, "end": v(5.5, 24.54) * mm});
            skLineSegment(sketch, "E63.1.0.16", {"start": v(5.5, -24.54) * mm, "end": v(9.25, -22.37) * mm});
            skLineSegment(sketch, "E63.1.0.17", {"start": v(13, 7.5) * mm, "end": v(13, 3.18) * mm});
            skLineSegment(sketch, "E63.1.0.18", {"start": v(13, 24.54) * mm, "end": v(9.25, 22.37) * mm});
            skLineSegment(sketch, "E63.1.0.19", {"start": v(5.5, -28.87) * mm, "end": v(5.5, -24.54) * mm});
            skLineSegment(sketch, "E63.1.0.20", {"start": v(9.25, 9.67) * mm, "end": v(13, 7.5) * mm});
            skLineSegment(sketch, "E63.1.0.21", {"start": v(5.5, -7.5) * mm, "end": v(5.5, -3.18) * mm});
            skLineSegment(sketch, "E63.1.0.22", {"start": v(9.25, -31.03) * mm, "end": v(5.5, -28.87) * mm});
            skLineSegment(sketch, "E63.1.0.23", {"start": v(5.5, 13.86) * mm, "end": v(5.5, 18.19) * mm});
            skLineSegment(sketch, "E63.1.0.24", {"start": v(13, 28.87) * mm, "end": v(13, 24.54) * mm});
            skLineSegment(sketch, "E63.1.0.25", {"start": v(5.5, -18.19) * mm, "end": v(5.5, -13.86) * mm});
            skLineSegment(sketch, "E63.1.0.26", {"start": v(13, 13.86) * mm, "end": v(9.25, 11.7) * mm});
            skLineSegment(sketch, "E63.1.0.27", {"start": v(13, 18.19) * mm, "end": v(13, 13.86) * mm});
            skLineSegment(sketch, "E63.1.0.28", {"start": v(5.5, -3.18) * mm, "end": v(9.25, -1.01) * mm});
            skLineSegment(sketch, "E63.1.0.29", {"start": v(5.5, 18.19) * mm, "end": v(9.25, 20.35) * mm});
            skLineSegment(sketch, "E63.1.0.30", {"start": v(9.25, 31.03) * mm, "end": v(13, 28.87) * mm});
            skLineSegment(sketch, "E63.1.0.31", {"start": v(5.5, -13.86) * mm, "end": v(9.25, -11.7) * mm});
            skLineSegment(sketch, "E63.1.0.32", {"start": v(9.25, -22.37) * mm, "end": v(13, -24.54) * mm});
            skLineSegment(sketch, "E63.1.0.33", {"start": v(5.5, 7.5) * mm, "end": v(9.25, 9.67) * mm});
            skLineSegment(sketch, "E63.1.0.34", {"start": v(9.25, -1.01) * mm, "end": v(13, -3.18) * mm});
            skLineSegment(sketch, "E63.1.0.35", {"start": v(9.25, 20.35) * mm, "end": v(13, 18.19) * mm});
            skLineSegment(sketch, "E63.2.0.0", {"start": v(31.5, -13.86) * mm, "end": v(31.5, -18.19) * mm});
            skLineSegment(sketch, "E63.2.0.1", {"start": v(27.75, -11.7) * mm, "end": v(31.5, -13.86) * mm});
            skLineSegment(sketch, "E63.2.0.2", {"start": v(24, 28.87) * mm, "end": v(27.75, 31.03) * mm});
            skLineSegment(sketch, "E63.2.0.3", {"start": v(27.75, -20.35) * mm, "end": v(24, -18.19) * mm});
            skLineSegment(sketch, "E63.2.0.4", {"start": v(31.5, -28.87) * mm, "end": v(27.75, -31.03) * mm});
            skLineSegment(sketch, "E63.2.0.5", {"start": v(24, 3.18) * mm, "end": v(24, 7.5) * mm});
            skLineSegment(sketch, "E63.2.0.6", {"start": v(27.75, 11.7) * mm, "end": v(24, 13.86) * mm});
            skLineSegment(sketch, "E63.2.0.7", {"start": v(24, 24.54) * mm, "end": v(24, 28.87) * mm});
            skLineSegment(sketch, "E63.2.0.8", {"start": v(31.5, -18.19) * mm, "end": v(27.75, -20.35) * mm});
            skLineSegment(sketch, "E63.2.0.9", {"start": v(27.75, -9.67) * mm, "end": v(24, -7.5) * mm});
            skLineSegment(sketch, "E63.2.0.10", {"start": v(31.5, -3.18) * mm, "end": v(31.5, -7.5) * mm});
            skLineSegment(sketch, "E63.2.0.11", {"start": v(31.5, 3.18) * mm, "end": v(27.75, 1.01) * mm});
            skLineSegment(sketch, "E63.2.0.12", {"start": v(31.5, -7.5) * mm, "end": v(27.75, -9.67) * mm});
            skLineSegment(sketch, "E63.2.0.13", {"start": v(31.5, -24.54) * mm, "end": v(31.5, -28.87) * mm});
            skLineSegment(sketch, "E63.2.0.14", {"start": v(27.75, 1.01) * mm, "end": v(24, 3.18) * mm});
            skLineSegment(sketch, "E63.2.0.15", {"start": v(27.75, 22.37) * mm, "end": v(24, 24.54) * mm});
            skLineSegment(sketch, "E63.2.0.16", {"start": v(24, -24.54) * mm, "end": v(27.75, -22.37) * mm});
            skLineSegment(sketch, "E63.2.0.17", {"start": v(31.5, 7.5) * mm, "end": v(31.5, 3.18) * mm});
            skLineSegment(sketch, "E63.2.0.18", {"start": v(31.5, 24.54) * mm, "end": v(27.75, 22.37) * mm});
            skLineSegment(sketch, "E63.2.0.19", {"start": v(24, -28.87) * mm, "end": v(24, -24.54) * mm});
            skLineSegment(sketch, "E63.2.0.20", {"start": v(27.75, 9.67) * mm, "end": v(31.5, 7.5) * mm});
            skLineSegment(sketch, "E63.2.0.21", {"start": v(24, -7.5) * mm, "end": v(24, -3.18) * mm});
            skLineSegment(sketch, "E63.2.0.22", {"start": v(27.75, -31.03) * mm, "end": v(24, -28.87) * mm});
            skLineSegment(sketch, "E63.2.0.23", {"start": v(24, 13.86) * mm, "end": v(24, 18.19) * mm});
            skLineSegment(sketch, "E63.2.0.24", {"start": v(31.5, 28.87) * mm, "end": v(31.5, 24.54) * mm});
            skLineSegment(sketch, "E63.2.0.25", {"start": v(24, -18.19) * mm, "end": v(24, -13.86) * mm});
            skLineSegment(sketch, "E63.2.0.26", {"start": v(31.5, 13.86) * mm, "end": v(27.75, 11.7) * mm});
            skLineSegment(sketch, "E63.2.0.27", {"start": v(31.5, 18.19) * mm, "end": v(31.5, 13.86) * mm});
            skLineSegment(sketch, "E63.2.0.28", {"start": v(24, -3.18) * mm, "end": v(27.75, -1.01) * mm});
            skLineSegment(sketch, "E63.2.0.29", {"start": v(24, 18.19) * mm, "end": v(27.75, 20.35) * mm});
            skLineSegment(sketch, "E63.2.0.30", {"start": v(27.75, 31.03) * mm, "end": v(31.5, 28.87) * mm});
            skLineSegment(sketch, "E63.2.0.31", {"start": v(24, -13.86) * mm, "end": v(27.75, -11.7) * mm});
            skLineSegment(sketch, "E63.2.0.32", {"start": v(27.75, -22.37) * mm, "end": v(31.5, -24.54) * mm});
            skLineSegment(sketch, "E63.2.0.33", {"start": v(24, 7.5) * mm, "end": v(27.75, 9.67) * mm});
            skLineSegment(sketch, "E63.2.0.34", {"start": v(27.75, -1.01) * mm, "end": v(31.5, -3.18) * mm});
            skLineSegment(sketch, "E63.2.0.35", {"start": v(27.75, 20.35) * mm, "end": v(31.5, 18.19) * mm});
            skLineSegment(sketch, "E63.direction1", {"start": v(-13, -28.87) * mm, "end": v(5.5, -28.87) * mm, "construction": true});
            skLineSegment(sketch, "E64.1.0.0", {"start": v(-18.5, -36.37) * mm, "end": v(-22.25, -34.2) * mm});
            skLineSegment(sketch, "E64.1.0.1", {"start": v(-14.75, -34.2) * mm, "end": v(-18.5, -36.37) * mm});
            skLineSegment(sketch, "E64.1.0.2", {"start": v(-14.75, 23.53) * mm, "end": v(-14.75, 19.2) * mm});
            skLineSegment(sketch, "E64.1.0.3", {"start": v(-27.75, -20.35) * mm, "end": v(-31.5, -18.19) * mm});
            skLineSegment(sketch, "E64.1.0.4", {"start": v(-31.5, 28.87) * mm, "end": v(-27.75, 31.03) * mm});
            skLineSegment(sketch, "E64.1.0.5", {"start": v(-24, 18.19) * mm, "end": v(-24, 13.86) * mm});
            skLineSegment(sketch, "E64.1.0.6", {"start": v(-31.5, 7.5) * mm, "end": v(-27.75, 9.67) * mm});
            skLineSegment(sketch, "E64.1.0.7", {"start": v(-24, -13.86) * mm, "end": v(-24, -18.19) * mm});
            skLineSegment(sketch, "E64.1.0.8", {"start": v(-18.5, -25.7) * mm, "end": v(-22.25, -23.53) * mm});
            skLineSegment(sketch, "E64.1.0.9", {"start": v(-24, -18.19) * mm, "end": v(-27.75, -20.35) * mm});
            skLineSegment(sketch, "E64.1.0.10", {"start": v(-18.5, 25.7) * mm, "end": v(-14.75, 23.53) * mm});
            skLineSegment(sketch, "E64.1.0.11", {"start": v(-14.75, -29.88) * mm, "end": v(-14.75, -34.2) * mm});
            skLineSegment(sketch, "E64.1.0.12", {"start": v(-27.75, -22.37) * mm, "end": v(-24, -24.54) * mm});
            skLineSegment(sketch, "E64.1.0.13", {"start": v(-24, 3.18) * mm, "end": v(-27.75, 1.01) * mm});
            skLineSegment(sketch, "E64.1.0.14", {"start": v(-18.5, -27.71) * mm, "end": v(-14.75, -29.88) * mm});
            skLineSegment(sketch, "E64.1.0.15", {"start": v(-14.75, 8.52) * mm, "end": v(-18.5, 6.35) * mm});
            skLineSegment(sketch, "E64.1.0.16", {"start": v(-22.25, -23.53) * mm, "end": v(-22.25, -19.2) * mm});
            skLineSegment(sketch, "E64.1.0.17", {"start": v(-14.75, 19.2) * mm, "end": v(-18.5, 17.03) * mm});
            skLineSegment(sketch, "E64.1.0.18", {"start": v(-24, 13.86) * mm, "end": v(-27.75, 11.7) * mm});
            skLineSegment(sketch, "E64.1.0.19", {"start": v(-27.75, 31.03) * mm, "end": v(-24, 28.87) * mm});
            skLineSegment(sketch, "E64.1.0.20", {"start": v(-22.25, 23.53) * mm, "end": v(-18.5, 25.7) * mm});
            skLineSegment(sketch, "E64.1.0.21", {"start": v(-27.75, 22.37) * mm, "end": v(-31.5, 24.54) * mm});
            skLineSegment(sketch, "E64.1.0.22", {"start": v(-18.5, 27.71) * mm, "end": v(-22.25, 29.88) * mm});
            skLineSegment(sketch, "E64.1.0.23", {"start": v(-24, 7.5) * mm, "end": v(-24, 3.18) * mm});
            skLineSegment(sketch, "E64.1.0.24", {"start": v(-31.5, -24.54) * mm, "end": v(-27.75, -22.37) * mm});
            skLineSegment(sketch, "E64.1.0.25", {"start": v(-22.25, -29.88) * mm, "end": v(-18.5, -27.71) * mm});
            skLineSegment(sketch, "E64.1.0.26", {"start": v(-14.75, 12.85) * mm, "end": v(-14.75, 8.52) * mm});
            skLineSegment(sketch, "E64.1.0.27", {"start": v(-14.75, 29.88) * mm, "end": v(-18.5, 27.71) * mm});
            skLineSegment(sketch, "E64.1.0.28", {"start": v(-24, -28.87) * mm, "end": v(-27.75, -31.03) * mm});
            skLineSegment(sketch, "E64.1.0.29", {"start": v(-27.75, -9.67) * mm, "end": v(-31.5, -7.5) * mm});
            skLineSegment(sketch, "E64.1.0.30", {"start": v(-31.5, -18.19) * mm, "end": v(-31.5, -13.86) * mm});
            skLineSegment(sketch, "E64.1.0.31", {"start": v(-27.75, 9.67) * mm, "end": v(-24, 7.5) * mm});
            skLineSegment(sketch, "E64.1.0.32", {"start": v(-22.25, -34.2) * mm, "end": v(-22.25, -29.88) * mm});
            skLineSegment(sketch, "E64.1.0.33", {"start": v(-22.25, 12.85) * mm, "end": v(-18.5, 15.01) * mm});
            skLineSegment(sketch, "E64.1.0.34", {"start": v(-27.75, -11.7) * mm, "end": v(-24, -13.86) * mm});
            skLineSegment(sketch, "E64.1.0.35", {"start": v(-31.5, 13.86) * mm, "end": v(-31.5, 18.19) * mm});
            skLineSegment(sketch, "E64.1.0.36", {"start": v(-31.5, -7.5) * mm, "end": v(-31.5, -3.18) * mm});
            skLineSegment(sketch, "E64.1.0.37", {"start": v(-18.5, -17.03) * mm, "end": v(-14.75, -19.2) * mm});
            skLineSegment(sketch, "E64.1.0.38", {"start": v(-22.25, 19.2) * mm, "end": v(-22.25, 23.53) * mm});
            skLineSegment(sketch, "E64.1.0.39", {"start": v(-18.5, 15.01) * mm, "end": v(-14.75, 12.85) * mm});
            skLineSegment(sketch, "E64.1.0.40", {"start": v(-31.5, 18.19) * mm, "end": v(-27.75, 20.35) * mm});
            skLineSegment(sketch, "E64.1.0.41", {"start": v(-31.5, -3.18) * mm, "end": v(-27.75, -1.01) * mm});
            skLineSegment(sketch, "E64.1.0.42", {"start": v(-14.75, -23.53) * mm, "end": v(-18.5, -25.7) * mm});
            skLineSegment(sketch, "E64.1.0.43", {"start": v(-27.75, 20.35) * mm, "end": v(-24, 18.19) * mm});
            skLineSegment(sketch, "E64.1.0.44", {"start": v(-27.75, -1.01) * mm, "end": v(-24, -3.18) * mm});
            skLineSegment(sketch, "E64.1.0.45", {"start": v(-31.5, -13.86) * mm, "end": v(-27.75, -11.7) * mm});
            skLineSegment(sketch, "E64.1.0.46", {"start": v(-27.75, 11.7) * mm, "end": v(-31.5, 13.86) * mm});
            skLineSegment(sketch, "E64.1.0.47", {"start": v(-22.25, -19.2) * mm, "end": v(-18.5, -17.03) * mm});
            skLineSegment(sketch, "E64.1.0.48", {"start": v(-18.5, 17.03) * mm, "end": v(-22.25, 19.2) * mm});
            skLineSegment(sketch, "E64.1.0.49", {"start": v(-22.25, -8.52) * mm, "end": v(-18.5, -6.35) * mm});
            skLineSegment(sketch, "E64.1.0.50", {"start": v(-22.25, -12.85) * mm, "end": v(-22.25, -8.52) * mm});
            skLineSegment(sketch, "E64.1.0.51", {"start": v(-18.5, -15.01) * mm, "end": v(-22.25, -12.85) * mm});
            skLineSegment(sketch, "E64.1.0.52", {"start": v(-14.75, -8.52) * mm, "end": v(-14.75, -12.85) * mm});
            skLineSegment(sketch, "E64.1.0.53", {"start": v(-18.5, 4.33) * mm, "end": v(-14.75, 2.17) * mm});
            skLineSegment(sketch, "E64.1.0.54", {"start": v(-22.25, 2.17) * mm, "end": v(-18.5, 4.33) * mm});
            skLineSegment(sketch, "E64.1.0.55", {"start": v(-22.25, -2.17) * mm, "end": v(-22.25, 2.17) * mm});
            skLineSegment(sketch, "E64.1.0.56", {"start": v(-18.5, -4.33) * mm, "end": v(-22.25, -2.17) * mm});
            skLineSegment(sketch, "E64.1.0.57", {"start": v(-14.75, -2.17) * mm, "end": v(-18.5, -4.33) * mm});
            skLineSegment(sketch, "E64.1.0.58", {"start": v(-14.75, 2.17) * mm, "end": v(-14.75, -2.17) * mm});
            skLineSegment(sketch, "E64.1.0.59", {"start": v(-14.75, -19.2) * mm, "end": v(-14.75, -23.53) * mm});
            skLineSegment(sketch, "E64.1.0.60", {"start": v(-18.5, -6.35) * mm, "end": v(-14.75, -8.52) * mm});
            skLineSegment(sketch, "E64.1.0.61", {"start": v(-24, -7.5) * mm, "end": v(-27.75, -9.67) * mm});
            skLineSegment(sketch, "E64.1.0.62", {"start": v(-27.75, 1.01) * mm, "end": v(-31.5, 3.18) * mm});
            skLineSegment(sketch, "E64.1.0.63", {"start": v(-18.5, 6.35) * mm, "end": v(-22.25, 8.52) * mm});
            skLineSegment(sketch, "E64.1.0.64", {"start": v(-24, 28.87) * mm, "end": v(-24, 24.54) * mm});
            skLineSegment(sketch, "E64.1.0.65", {"start": v(-31.5, 24.54) * mm, "end": v(-31.5, 28.87) * mm});
            skLineSegment(sketch, "E64.1.0.66", {"start": v(-31.5, 3.18) * mm, "end": v(-31.5, 7.5) * mm});
            skLineSegment(sketch, "E64.1.0.67", {"start": v(-24, -3.18) * mm, "end": v(-24, -7.5) * mm});
            skLineSegment(sketch, "E64.1.0.68", {"start": v(-24, 24.54) * mm, "end": v(-27.75, 22.37) * mm});
            skLineSegment(sketch, "E64.1.0.69", {"start": v(-22.25, 8.52) * mm, "end": v(-22.25, 12.85) * mm});
            skLineSegment(sketch, "E64.1.0.70", {"start": v(-31.5, -28.87) * mm, "end": v(-31.5, -24.54) * mm});
            skLineSegment(sketch, "E64.1.0.71", {"start": v(-27.75, -31.03) * mm, "end": v(-31.5, -28.87) * mm});
            skLineSegment(sketch, "E64.1.0.72", {"start": v(-14.75, -12.85) * mm, "end": v(-18.5, -15.01) * mm});
            skLineSegment(sketch, "E64.1.0.73", {"start": v(-24, -24.54) * mm, "end": v(-24, -28.87) * mm});
            skLineSegment(sketch, "E64.1.0.74", {"start": v(-22.25, 29.88) * mm, "end": v(-22.25, 34.2) * mm});
            skLineSegment(sketch, "E64.1.0.75", {"start": v(-22.25, 34.2) * mm, "end": v(-18.5, 36.37) * mm});
            skLineSegment(sketch, "E64.1.0.76", {"start": v(-18.5, 36.37) * mm, "end": v(-14.75, 34.2) * mm});
            skLineSegment(sketch, "E64.1.0.77", {"start": v(-14.75, 34.2) * mm, "end": v(-14.75, 29.88) * mm});
            skLineSegment(sketch, "E64.2.0.2", {"start": v(-33.25, 23.53) * mm, "end": v(-33.25, 19.2) * mm});
            skLineSegment(sketch, "E64.2.0.8", {"start": v(-37, -25.7) * mm, "end": v(-40.75, -23.53) * mm});
            skLineSegment(sketch, "E64.2.0.10", {"start": v(-37, 25.7) * mm, "end": v(-33.25, 23.53) * mm});
            skLineSegment(sketch, "E64.2.0.15", {"start": v(-33.25, 8.52) * mm, "end": v(-37, 6.35) * mm});
            skLineSegment(sketch, "E64.2.0.16", {"start": v(-40.75, -23.53) * mm, "end": v(-40.75, -19.2) * mm});
            skLineSegment(sketch, "E64.2.0.17", {"start": v(-33.25, 19.2) * mm, "end": v(-37, 17.03) * mm});
            skLineSegment(sketch, "E64.2.0.20", {"start": v(-40.75, 23.53) * mm, "end": v(-37, 25.7) * mm});
            skLineSegment(sketch, "E64.2.0.26", {"start": v(-33.25, 12.85) * mm, "end": v(-33.25, 8.52) * mm});
            skLineSegment(sketch, "E64.2.0.33", {"start": v(-40.75, 12.85) * mm, "end": v(-37, 15.01) * mm});
            skLineSegment(sketch, "E64.2.0.37", {"start": v(-37, -17.03) * mm, "end": v(-33.25, -19.2) * mm});
            skLineSegment(sketch, "E64.2.0.38", {"start": v(-40.75, 19.2) * mm, "end": v(-40.75, 23.53) * mm});
            skLineSegment(sketch, "E64.2.0.39", {"start": v(-37, 15.01) * mm, "end": v(-33.25, 12.85) * mm});
            skLineSegment(sketch, "E64.2.0.42", {"start": v(-33.25, -23.53) * mm, "end": v(-37, -25.7) * mm});
            skLineSegment(sketch, "E64.2.0.47", {"start": v(-40.75, -19.2) * mm, "end": v(-37, -17.03) * mm});
            skLineSegment(sketch, "E64.2.0.48", {"start": v(-37, 17.03) * mm, "end": v(-40.75, 19.2) * mm});
            skLineSegment(sketch, "E64.2.0.49", {"start": v(-40.75, -8.52) * mm, "end": v(-37, -6.35) * mm});
            skLineSegment(sketch, "E64.2.0.50", {"start": v(-40.75, -12.85) * mm, "end": v(-40.75, -8.52) * mm});
            skLineSegment(sketch, "E64.2.0.51", {"start": v(-37, -15.01) * mm, "end": v(-40.75, -12.85) * mm});
            skLineSegment(sketch, "E64.2.0.52", {"start": v(-33.25, -8.52) * mm, "end": v(-33.25, -12.85) * mm});
            skLineSegment(sketch, "E64.2.0.53", {"start": v(-37, 4.33) * mm, "end": v(-33.25, 2.17) * mm});
            skLineSegment(sketch, "E64.2.0.54", {"start": v(-40.75, 2.17) * mm, "end": v(-37, 4.33) * mm});
            skLineSegment(sketch, "E64.2.0.55", {"start": v(-40.75, -2.17) * mm, "end": v(-40.75, 2.17) * mm});
            skLineSegment(sketch, "E64.2.0.56", {"start": v(-37, -4.33) * mm, "end": v(-40.75, -2.17) * mm});
            skLineSegment(sketch, "E64.2.0.57", {"start": v(-33.25, -2.17) * mm, "end": v(-37, -4.33) * mm});
            skLineSegment(sketch, "E64.2.0.58", {"start": v(-33.25, 2.17) * mm, "end": v(-33.25, -2.17) * mm});
            skLineSegment(sketch, "E64.2.0.59", {"start": v(-33.25, -19.2) * mm, "end": v(-33.25, -23.53) * mm});
            skLineSegment(sketch, "E64.2.0.60", {"start": v(-37, -6.35) * mm, "end": v(-33.25, -8.52) * mm});
            skLineSegment(sketch, "E64.2.0.63", {"start": v(-37, 6.35) * mm, "end": v(-40.75, 8.52) * mm});
            skLineSegment(sketch, "E64.2.0.69", {"start": v(-40.75, 8.52) * mm, "end": v(-40.75, 12.85) * mm});
            skLineSegment(sketch, "E64.2.0.72", {"start": v(-33.25, -12.85) * mm, "end": v(-37, -15.01) * mm});
            skLineSegment(sketch, "E64.direction1", {"start": v(-13, -28.87) * mm, "end": v(-31.5, -28.87) * mm, "construction": true});
            skLineSegment(sketch, "E65.1.0.0", {"start": v(5.5, 39.55) * mm, "end": v(9.25, 41.71) * mm});
            skLineSegment(sketch, "E65.1.0.1", {"start": v(5.5, 35.22) * mm, "end": v(5.5, 39.55) * mm});
            skLineSegment(sketch, "E65.1.0.2", {"start": v(9.25, 33.05) * mm, "end": v(5.5, 35.22) * mm});
            skLineSegment(sketch, "E65.1.0.3", {"start": v(13, 35.22) * mm, "end": v(9.25, 33.05) * mm});
            skLineSegment(sketch, "E65.1.0.4", {"start": v(13, 39.55) * mm, "end": v(13, 35.22) * mm});
            skLineSegment(sketch, "E65.1.0.5", {"start": v(9.25, 41.71) * mm, "end": v(13, 39.55) * mm});
            skLineSegment(sketch, "E65.1.0.6", {"start": v(9.25, -41.71) * mm, "end": v(5.5, -39.55) * mm});
            skLineSegment(sketch, "E65.1.0.7", {"start": v(13, -39.55) * mm, "end": v(9.25, -41.71) * mm});
            skLineSegment(sketch, "E65.1.0.8", {"start": v(13, -35.22) * mm, "end": v(13, -39.55) * mm});
            skLineSegment(sketch, "E65.1.0.9", {"start": v(9.25, -33.05) * mm, "end": v(13, -35.22) * mm});
            skLineSegment(sketch, "E65.1.0.10", {"start": v(5.5, -35.22) * mm, "end": v(9.25, -33.05) * mm});
            skLineSegment(sketch, "E65.1.0.11", {"start": v(5.5, -39.55) * mm, "end": v(5.5, -35.22) * mm});
            skLineSegment(sketch, "E65.direction1", {"start": v(-13, -39.55) * mm, "end": v(5.5, -39.55) * mm, "construction": true});
            skSolve(sketch);
        }
        {
            var Q0;
            Q0=makeQuery(id+"F5.imprint","IMPRINT",FACE,{"disambiguationData":[TD([[makeQuery(id+"F5.imprint","IMPRINT",EDGE,{"derivedFrom":sQuery(id+"F5.wireOp",EDGE,"E26.0")}),-1.0]])]});
            var Q1;
            Q1=makeQuery(id+"F5.imprint","IMPRINT",FACE,{"disambiguationData":[TD([[makeQuery(id+"F5.imprint","IMPRINT",EDGE,{"derivedFrom":sQuery(id+"F5.wireOp",EDGE,"E27.0")}),-1.0]])]});
            var Q2;
            Q2=makeQuery(id+"F5.imprint","IMPRINT",FACE,{"disambiguationData":[TD([[makeQuery(id+"F5.imprint","IMPRINT",EDGE,{"derivedFrom":sQuery(id+"F5.wireOp",EDGE,"E28.0")}),-1.0]])]});
            var Q3;
            Q3=makeQuery(id+"F5.imprint","IMPRINT",FACE,{"disambiguationData":[TD([[makeQuery(id+"F5.imprint","IMPRINT",EDGE,{"derivedFrom":sQuery(id+"F5.wireOp",EDGE,"E29.0")}),-1.0]])]});
            var Q4;
            Q4=makeQuery(id+"F5.imprint","IMPRINT",FACE,{"disambiguationData":[TD([[makeQuery(id+"F5.imprint","IMPRINT",EDGE,{"derivedFrom":sQuery(id+"F5.wireOp",EDGE,"E48.0")}),-1.0]])]});
            var Q5;
            Q5=makeQuery(id+"F5.imprint","IMPRINT",FACE,{"disambiguationData":[TD([[makeQuery(id+"F5.imprint","IMPRINT",EDGE,{"derivedFrom":sQuery(id+"F5.wireOp",EDGE,"E47.0")}),-1.0]])]});
            var Q6;
            Q6=makeQuery(id+"F5.imprint","IMPRINT",FACE,{"disambiguationData":[TD([[makeQuery(id+"F5.imprint","IMPRINT",EDGE,{"derivedFrom":sQuery(id+"F5.wireOp",EDGE,"E46.0")}),-1.0]])]});
            var Q7;
            Q7=makeQuery(id+"F5.imprint","IMPRINT",FACE,{"disambiguationData":[TD([[makeQuery(id+"F5.imprint","IMPRINT",EDGE,{"derivedFrom":sQuery(id+"F5.wireOp",EDGE,"E50.0")}),-1.0]])]});
            var Q8;
            Q8=makeQuery(id+"F5.imprint","IMPRINT",FACE,{"disambiguationData":[TD([[makeQuery(id+"F5.imprint","IMPRINT",EDGE,{"derivedFrom":sQuery(id+"F5.wireOp",EDGE,"E51.0")}),-1.0]])]});
            var Q9;
            Q9=makeQuery(id+"F5.imprint","IMPRINT",FACE,{"disambiguationData":[TD([[makeQuery(id+"F5.imprint","IMPRINT",EDGE,{"derivedFrom":sQuery(id+"F5.wireOp",EDGE,"E37.0")}),-1.0]])]});
            var Q10;
            Q10=makeQuery(id+"F5.imprint","IMPRINT",FACE,{"disambiguationData":[TD([[makeQuery(id+"F5.imprint","IMPRINT",EDGE,{"derivedFrom":sQuery(id+"F5.wireOp",EDGE,"E38.0")}),-1.0]])]});
            var Q11;
            Q11=makeQuery(id+"F5.imprint","IMPRINT",FACE,{"disambiguationData":[TD([[makeQuery(id+"F5.imprint","IMPRINT",EDGE,{"derivedFrom":sQuery(id+"F5.wireOp",EDGE,"E52.0")}),-1.0]])]});
            var Q12;
            Q12=makeQuery(id+"F5.imprint","IMPRINT",FACE,{"disambiguationData":[TD([[makeQuery(id+"F5.imprint","IMPRINT",EDGE,{"derivedFrom":sQuery(id+"F5.wireOp",EDGE,"E39.0")}),-1.0]])]});
            var Q13;
            Q13=makeQuery(id+"F5.imprint","IMPRINT",FACE,{"disambiguationData":[TD([[makeQuery(id+"F5.imprint","IMPRINT",EDGE,{"derivedFrom":sQuery(id+"F5.wireOp",EDGE,"E62.1.0.6")}),-1.0]])]});
            var Q14;
            Q14=makeQuery(id+"F5.imprint","IMPRINT",FACE,{"disambiguationData":[TD([[makeQuery(id+"F5.imprint","IMPRINT",EDGE,{"derivedFrom":sQuery(id+"F5.wireOp",EDGE,"E62.1.0.2")}),-1.0]])]});
            var Q15;
            Q15=makeQuery(id+"F5.imprint","IMPRINT",FACE,{"disambiguationData":[TD([[makeQuery(id+"F5.imprint","IMPRINT",EDGE,{"derivedFrom":sQuery(id+"F5.wireOp",EDGE,"E62.1.0.3")}),-1.0]])]});
            var Q16;
            Q16=makeQuery(id+"F5.imprint","IMPRINT",FACE,{"disambiguationData":[TD([[makeQuery(id+"F5.imprint","IMPRINT",EDGE,{"derivedFrom":sQuery(id+"F5.wireOp",EDGE,"E62.1.0.5")}),-1.0]])]});
            var Q17;
            Q17=makeQuery(id+"F5.imprint","IMPRINT",FACE,{"disambiguationData":[TD([[makeQuery(id+"F5.imprint","IMPRINT",EDGE,{"derivedFrom":sQuery(id+"F5.wireOp",EDGE,"E62.1.0.8")}),-1.0]])]});
            var Q18;
            Q18=makeQuery(id+"F5.imprint","IMPRINT",FACE,{"disambiguationData":[TD([[makeQuery(id+"F5.imprint","IMPRINT",EDGE,{"derivedFrom":sQuery(id+"F5.wireOp",EDGE,"E62.2.0.8")}),-1.0]])]});
            var Q19;
            Q19=makeQuery(id+"F5.imprint","IMPRINT",FACE,{"disambiguationData":[TD([[makeQuery(id+"F5.imprint","IMPRINT",EDGE,{"derivedFrom":sQuery(id+"F5.wireOp",EDGE,"E62.2.0.5")}),-1.0]])]});
            var Q20;
            Q20=makeQuery(id+"F5.imprint","IMPRINT",FACE,{"disambiguationData":[TD([[makeQuery(id+"F5.imprint","IMPRINT",EDGE,{"derivedFrom":sQuery(id+"F5.wireOp",EDGE,"E62.2.0.3")}),-1.0]])]});
            var Q21;
            Q21=makeQuery(id+"F5.imprint","IMPRINT",FACE,{"disambiguationData":[TD([[makeQuery(id+"F5.imprint","IMPRINT",EDGE,{"derivedFrom":sQuery(id+"F5.wireOp",EDGE,"E62.2.0.2")}),-1.0]])]});
            var Q22;
            Q22=makeQuery(id+"F5.imprint","IMPRINT",FACE,{"disambiguationData":[TD([[makeQuery(id+"F5.imprint","IMPRINT",EDGE,{"derivedFrom":sQuery(id+"F5.wireOp",EDGE,"E62.2.0.6")}),-1.0]])]});
            var Q23;
            Q23=makeQuery(id+"F5.imprint","IMPRINT",FACE,{"disambiguationData":[TD([[makeQuery(id+"F5.imprint","IMPRINT",EDGE,{"derivedFrom":sQuery(id+"F5.wireOp",EDGE,"E64.1.0.2")}),-1.0]])]});
            var Q24;
            Q24=makeQuery(id+"F5.imprint","IMPRINT",FACE,{"disambiguationData":[TD([[makeQuery(id+"F5.imprint","IMPRINT",EDGE,{"derivedFrom":sQuery(id+"F5.wireOp",EDGE,"E64.1.0.15")}),-1.0]])]});
            var Q25;
            Q25=makeQuery(id+"F5.imprint","IMPRINT",FACE,{"disambiguationData":[TD([[makeQuery(id+"F5.imprint","IMPRINT",EDGE,{"derivedFrom":sQuery(id+"F5.wireOp",EDGE,"E64.1.0.53")}),-1.0]])]});
            var Q26;
            Q26=makeQuery(id+"F5.imprint","IMPRINT",FACE,{"disambiguationData":[TD([[makeQuery(id+"F5.imprint","IMPRINT",EDGE,{"derivedFrom":sQuery(id+"F5.wireOp",EDGE,"E64.1.0.49")}),-1.0]])]});
            var Q27;
            Q27=makeQuery(id+"F5.imprint","IMPRINT",FACE,{"disambiguationData":[TD([[makeQuery(id+"F5.imprint","IMPRINT",EDGE,{"derivedFrom":sQuery(id+"F5.wireOp",EDGE,"E64.1.0.8")}),-1.0]])]});
            var Q28;
            {var subQ0=sQuery(id+"F5.wireOp",EDGE,"E64.1.0.11");Q28=makeQuery(id+"F5.imprint","IMPRINT",FACE,{"disambiguationData":[TD([[makeQuery(id+"F5.imprint","IMPRINT",EDGE,{"derivedFrom":subQ0}),-1.0]])]});}
            var Q29;
            Q29=makeQuery(id+"F5.imprint","IMPRINT",FACE,{"disambiguationData":[TD([[makeQuery(id+"F5.imprint","IMPRINT",EDGE,{"derivedFrom":sQuery(id+"F5.wireOp",EDGE,"E64.1.0.12")}),-1.0]])]});
            var Q30;
            Q30=makeQuery(id+"F5.imprint","IMPRINT",FACE,{"disambiguationData":[TD([[makeQuery(id+"F5.imprint","IMPRINT",EDGE,{"derivedFrom":sQuery(id+"F5.wireOp",EDGE,"E64.1.0.3")}),-1.0]])]});
            var Q31;
            Q31=makeQuery(id+"F5.imprint","IMPRINT",FACE,{"disambiguationData":[TD([[makeQuery(id+"F5.imprint","IMPRINT",EDGE,{"derivedFrom":sQuery(id+"F5.wireOp",EDGE,"E64.1.0.29")}),-1.0]])]});
            var Q32;
            Q32=makeQuery(id+"F5.imprint","IMPRINT",FACE,{"disambiguationData":[TD([[makeQuery(id+"F5.imprint","IMPRINT",EDGE,{"derivedFrom":sQuery(id+"F5.wireOp",EDGE,"E64.1.0.6")}),-1.0]])]});
            var Q33;
            Q33=makeQuery(id+"F5.imprint","IMPRINT",FACE,{"disambiguationData":[TD([[makeQuery(id+"F5.imprint","IMPRINT",EDGE,{"derivedFrom":sQuery(id+"F5.wireOp",EDGE,"E64.1.0.5")}),-1.0]])]});
            var Q34;
            {var subQ0=sQuery(id+"F5.wireOp",EDGE,"E64.2.0.2");Q34=makeQuery(id+"F5.imprint","IMPRINT",FACE,{"disambiguationData":[TD([[makeQuery(id+"F5.imprint","IMPRINT",EDGE,{"derivedFrom":subQ0}),-1.0]])]});}
            var Q35;
            {var subQ0=sQuery(id+"F5.wireOp",EDGE,"E64.2.0.15");Q35=makeQuery(id+"F5.imprint","IMPRINT",FACE,{"disambiguationData":[TD([[makeQuery(id+"F5.imprint","IMPRINT",EDGE,{"derivedFrom":subQ0}),-1.0]])]});}
            var Q36;
            {var subQ0=sQuery(id+"F5.wireOp",EDGE,"E64.2.0.53");Q36=makeQuery(id+"F5.imprint","IMPRINT",FACE,{"disambiguationData":[TD([[makeQuery(id+"F5.imprint","IMPRINT",EDGE,{"derivedFrom":subQ0}),-1.0]])]});}
            var Q37;
            Q37=makeQuery(id+"F5.imprint","IMPRINT",FACE,{"disambiguationData":[TD([[makeQuery(id+"F5.imprint","IMPRINT",EDGE,{"derivedFrom":sQuery(id+"F5.wireOp",EDGE,"E64.2.0.52")}),-1.0]])]});
            var Q38;
            {var subQ0=sQuery(id+"F5.wireOp",EDGE,"E64.2.0.37");Q38=makeQuery(id+"F5.imprint","IMPRINT",FACE,{"disambiguationData":[TD([[makeQuery(id+"F5.imprint","IMPRINT",EDGE,{"derivedFrom":subQ0}),-1.0]])]});}
            var Q39;
            {var subQ0=sQuery(id+"F5.wireOp",EDGE,"E64.1.0.21");Q39=makeQuery(id+"F5.imprint","IMPRINT",FACE,{"disambiguationData":[TD([[makeQuery(id+"F5.imprint","IMPRINT",EDGE,{"derivedFrom":subQ0}),-1.0]])]});}
            var Q40;
            {var subQ0=sQuery(id+"F5.wireOp",EDGE,"E64.1.0.22");Q40=makeQuery(id+"F5.imprint","IMPRINT",FACE,{"disambiguationData":[TD([[makeQuery(id+"F5.imprint","IMPRINT",EDGE,{"derivedFrom":subQ0}),-1.0]])]});}
            var Q41;
            {var subQ0=sQuery(id+"F5.wireOp",EDGE,"E65.1.0.1");Q41=makeQuery(id+"F5.imprint","IMPRINT",FACE,{"disambiguationData":[TD([[makeQuery(id+"F5.imprint","IMPRINT",EDGE,{"derivedFrom":subQ0}),-1.0]])]});}
            var Q42;
            Q42=makeQuery(id+"F5.imprint","IMPRINT",FACE,{"disambiguationData":[TD([[makeQuery(id+"F5.imprint","IMPRINT",EDGE,{"derivedFrom":sQuery(id+"F5.wireOp",EDGE,"E63.1.0.2")}),-1.0]])]});
            var Q43;
            Q43=makeQuery(id+"F5.imprint","IMPRINT",FACE,{"disambiguationData":[TD([[makeQuery(id+"F5.imprint","IMPRINT",EDGE,{"derivedFrom":sQuery(id+"F5.wireOp",EDGE,"E63.1.0.6")}),-1.0]])]});
            var Q44;
            Q44=makeQuery(id+"F5.imprint","IMPRINT",FACE,{"disambiguationData":[TD([[makeQuery(id+"F5.imprint","IMPRINT",EDGE,{"derivedFrom":sQuery(id+"F5.wireOp",EDGE,"E63.1.0.5")}),-1.0]])]});
            var Q45;
            Q45=makeQuery(id+"F5.imprint","IMPRINT",FACE,{"disambiguationData":[TD([[makeQuery(id+"F5.imprint","IMPRINT",EDGE,{"derivedFrom":sQuery(id+"F5.wireOp",EDGE,"E63.1.0.9")}),-1.0]])]});
            var Q46;
            Q46=makeQuery(id+"F5.imprint","IMPRINT",FACE,{"disambiguationData":[TD([[makeQuery(id+"F5.imprint","IMPRINT",EDGE,{"derivedFrom":sQuery(id+"F5.wireOp",EDGE,"E63.1.0.0")}),-1.0]])]});
            var Q47;
            Q47=makeQuery(id+"F5.imprint","IMPRINT",FACE,{"disambiguationData":[TD([[makeQuery(id+"F5.imprint","IMPRINT",EDGE,{"derivedFrom":sQuery(id+"F5.wireOp",EDGE,"E63.1.0.4")}),-1.0]])]});
            var Q48;
            {var subQ0=sQuery(id+"F5.wireOp",EDGE,"E65.1.0.9");Q48=makeQuery(id+"F5.imprint","IMPRINT",FACE,{"disambiguationData":[TD([[makeQuery(id+"F5.imprint","IMPRINT",EDGE,{"derivedFrom":subQ0}),-1.0]])]});}
            var Q49;
            {var subQ0=sQuery(id+"F5.wireOp",EDGE,"E62.1.0.18");Q49=makeQuery(id+"F5.imprint","IMPRINT",FACE,{"disambiguationData":[TD([[makeQuery(id+"F5.imprint","IMPRINT",EDGE,{"derivedFrom":subQ0}),-1.0]])]});}
            var Q50;
            Q50=makeQuery(id+"F5.imprint","IMPRINT",FACE,{"disambiguationData":[TD([[makeQuery(id+"F5.imprint","IMPRINT",EDGE,{"derivedFrom":sQuery(id+"F5.wireOp",EDGE,"E63.2.0.16")}),-1.0]])]});
            var Q51;
            Q51=makeQuery(id+"F5.imprint","IMPRINT",FACE,{"disambiguationData":[TD([[makeQuery(id+"F5.imprint","IMPRINT",EDGE,{"derivedFrom":sQuery(id+"F5.wireOp",EDGE,"E63.2.0.0")}),-1.0]])]});
            var Q52;
            Q52=makeQuery(id+"F5.imprint","IMPRINT",FACE,{"disambiguationData":[TD([[makeQuery(id+"F5.imprint","IMPRINT",EDGE,{"derivedFrom":sQuery(id+"F5.wireOp",EDGE,"E63.2.0.9")}),-1.0]])]});
            var Q53;
            Q53=makeQuery(id+"F5.imprint","IMPRINT",FACE,{"disambiguationData":[TD([[makeQuery(id+"F5.imprint","IMPRINT",EDGE,{"derivedFrom":sQuery(id+"F5.wireOp",EDGE,"E63.2.0.5")}),-1.0]])]});
            var Q54;
            Q54=makeQuery(id+"F5.imprint","IMPRINT",FACE,{"disambiguationData":[TD([[makeQuery(id+"F5.imprint","IMPRINT",EDGE,{"derivedFrom":sQuery(id+"F5.wireOp",EDGE,"E63.2.0.6")}),-1.0]])]});
            var Q55;
            {var subQ0=sQuery(id+"F5.wireOp",EDGE,"E63.2.0.7");Q55=makeQuery(id+"F5.imprint","IMPRINT",FACE,{"disambiguationData":[TD([[makeQuery(id+"F5.imprint","IMPRINT",EDGE,{"derivedFrom":subQ0}),-1.0]])]});}
            var Q56;
            {var subQ0=sQuery(id+"F5.wireOp",EDGE,"E53.3");Q56=makeQuery(id+"F5.imprint","IMPRINT",FACE,{"disambiguationData":[TD([[makeQuery(id+"F5.imprint","IMPRINT",EDGE,{"derivedFrom":subQ0}),-1.0]])]});}
            var Q57;
            {var subQ0=sQuery(id+"F5.wireOp",EDGE,"E40.1");Q57=makeQuery(id+"F5.imprint","IMPRINT",FACE,{"disambiguationData":[TD([[makeQuery(id+"F5.imprint","IMPRINT",EDGE,{"derivedFrom":subQ0}),-1.0]])]});}
            var Q58;
            Q58=makeQuery(id+"F5.imprint","IMPRINT",FACE,{"disambiguationData":[TD([[makeQuery(id+"F5.imprint","IMPRINT",EDGE,{"derivedFrom":sQuery(id+"F5.wireOp",EDGE,"E62.1.0.7")}),-1.0]])]});
            var Q59;
            {var subQ0=sQuery(id+"F5.wireOp",EDGE,"E49.1");Q59=makeQuery(id+"F5.imprint","IMPRINT",FACE,{"disambiguationData":[TD([[makeQuery(id+"F5.imprint","IMPRINT",EDGE,{"derivedFrom":subQ0}),-1.0]])]});}
            var Q60;
            {var subQ0=sQuery(id+"F5.wireOp",EDGE,"E30.4");Q60=makeQuery(id+"F5.imprint","IMPRINT",FACE,{"disambiguationData":[TD([[makeQuery(id+"F5.imprint","IMPRINT",EDGE,{"derivedFrom":subQ0}),-1.0]])]});}
            extrude(context, id + "F6", {"entities" : qUnion([Q0, Q1, Q2, Q3, Q4, Q5, Q6, Q7, Q8, Q9, Q10, Q11, Q12, Q13, Q14, Q15, Q16, Q17, Q18, Q19, Q20, Q21, Q22, Q23, Q24, Q25, Q26, Q27, Q28, Q29, Q30, Q31, Q32, Q33, Q34, Q35, Q36, Q37, Q38, Q39, Q40, Q41, Q42, Q43, Q44, Q45, Q46, Q47, Q48, Q49, Q50, Q51, Q52, Q53, Q54, Q55, Q56, Q57, Q58, Q59, Q60]), "operationType" : NewBodyOperationType.ADD, "depth" : 1.5 * mm});
        }
    });
